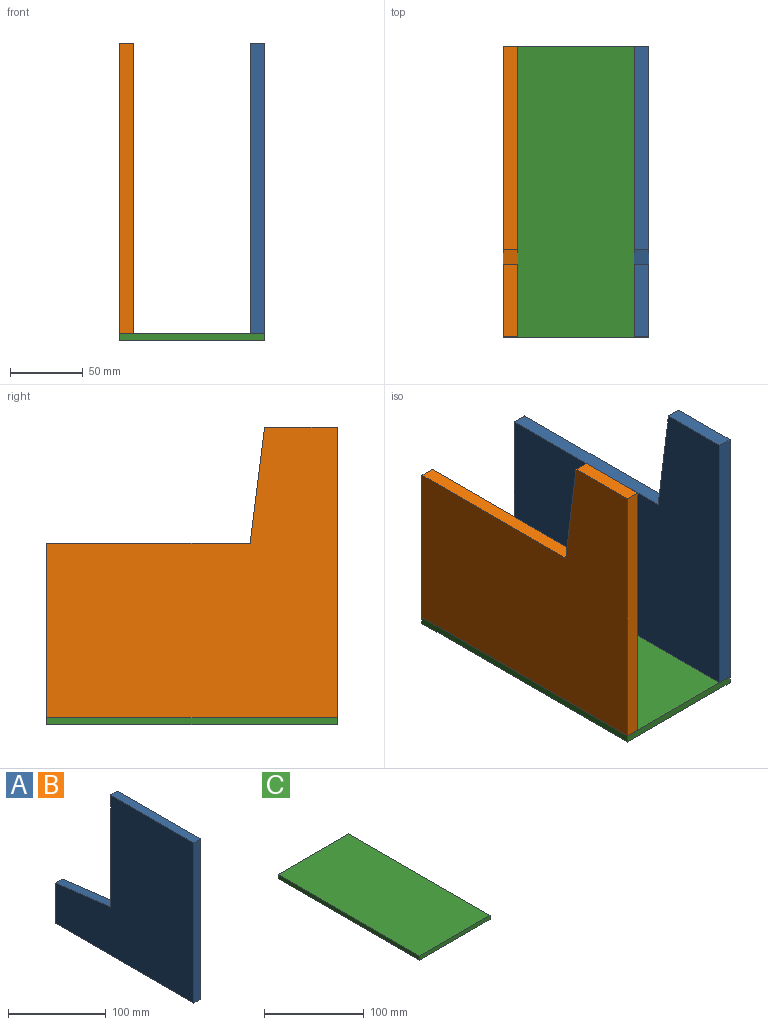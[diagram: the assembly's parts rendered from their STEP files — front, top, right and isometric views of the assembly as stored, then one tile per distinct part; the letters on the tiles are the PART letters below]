
ASSEMBLY  parts=3 mates=1
PART A: 8 faces, bbox 10x200x200 mm
  f0: plane 80x10mm, normal (0,0.12,0.99), area 806.2mm2, adj f1,f5,f6,f7
  f1: plane 140x10mm, normal (0,1,0), area 1400mm2, adj f0,f2,f6,f7
  f2: plane 120x10mm, normal (0,0,1), area 1200mm2, adj f1,f3,f6,f7
  f3: plane 200x10mm, normal (0,-1,0), area 2000mm2, adj f2,f4,f6,f7
  f4: plane 200x10mm, normal (0,0,-1), area 2000mm2, adj f3,f5,f6,f7
  f5: plane 50x10mm, normal (0,1,0), area 500mm2, adj f0,f4,f6,f7
  f6: plane 200x200mm, normal (1,0,0), area 28400mm2, adj f0,f1,f2,f3,f4,f5
  f7: plane 200x200mm, normal (-1,0,0), area 28400mm2, adj f0,f1,f2,f3,f4,f5
PART B: same geometry as A
PART C: 6 faces, bbox 100x200x5 mm
  f0: plane 200x5mm, normal (-1,0,0), area 1000mm2, adj f1,f3,f4,f5
  f1: plane 100x5mm, normal (0,-1,0), area 500mm2, adj f0,f2,f4,f5
  f2: plane 200x5mm, normal (1,0,0), area 1000mm2, adj f1,f3,f4,f5
  f3: plane 100x5mm, normal (0,1,0), area 500mm2, adj f0,f2,f4,f5
  f4: plane 200x100mm, normal (0,0,1), area 20000mm2, adj f0,f1,f2,f3
  f5: plane 200x100mm, normal (0,0,-1), area 20000mm2, adj f0,f1,f2,f3
PLACE A rot(axis=(0,0.71,0.71),180deg) t=(45,0,0)mm
PLACE B rot(axis=(0,0.71,0.71),180deg) t=(-45,0,0)mm
PLACE C rot(axis=(1,0,0),180deg) t=(0,100,0)mm
MATE fastened C.f5 <-> B.f3  axis (0,0,1) through (-50,200,0)mm
